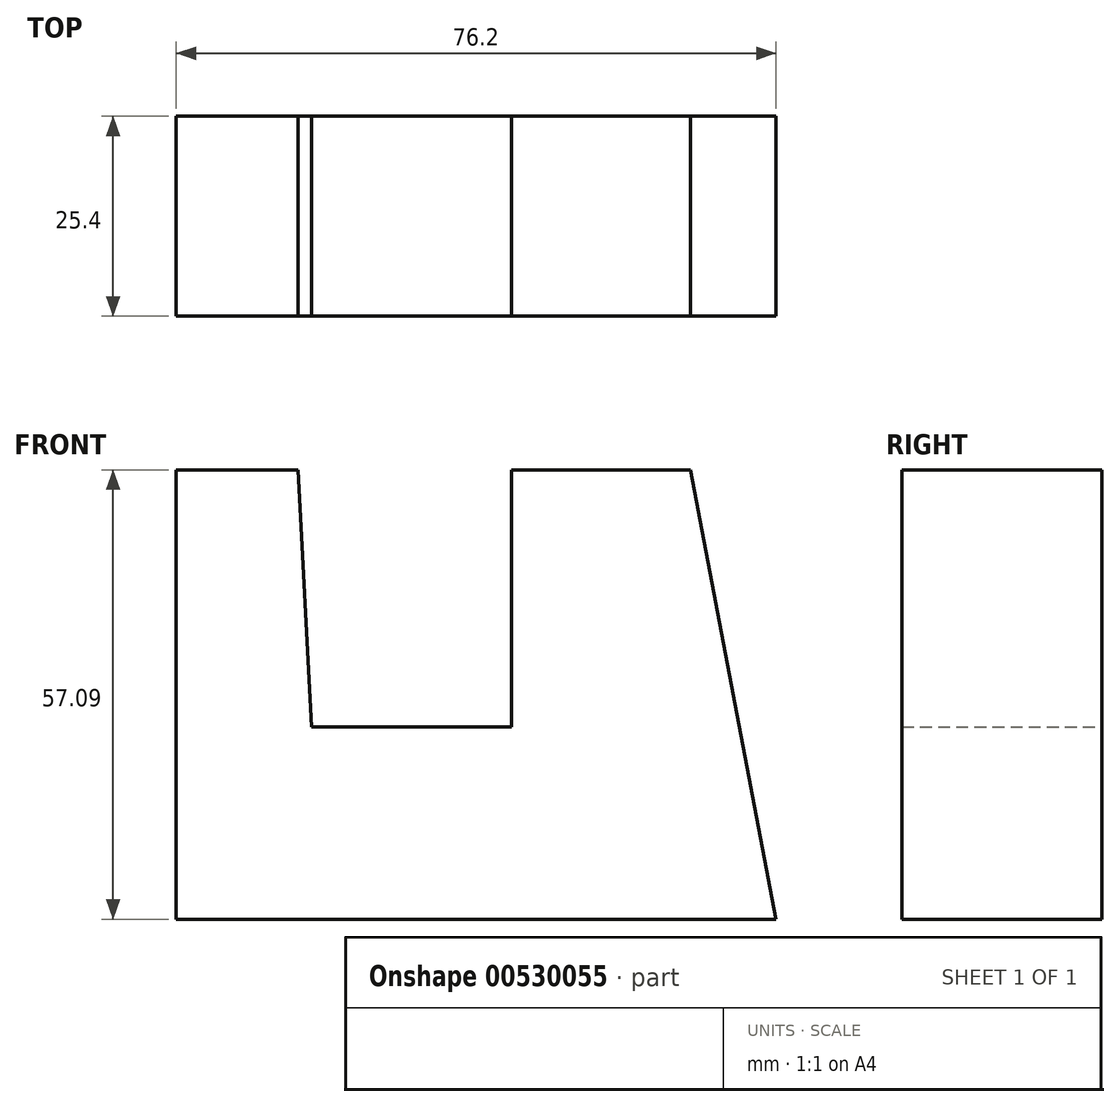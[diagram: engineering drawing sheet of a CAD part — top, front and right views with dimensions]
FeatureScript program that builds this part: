
annotation { "Feature Type Name" : "Feature", "Feature Type Description" : "" }
export const myFeature = defineFeature(function(context is Context, id is Id, definition is map)
    precondition{}
    {
        {
            var Q0;
            Q0=qCreatedBy(makeId("Front.planeOp"),FACE);
            var sketch = newSketch(context, id + "F0", { "sketchPlane" : qUnion([Q0])});
            skLineSegment(sketch, "E0", {"start": v(0, 0) * mm, "end": v(-76.2, 0) * mm});
            skLineSegment(sketch, "E1", {"start": v(-76.2, 0) * mm, "end": v(-76.2, 57.09) * mm});
            skLineSegment(sketch, "E2", {"start": v(-76.2, 57.09) * mm, "end": v(-60.72, 57.09) * mm});
            skLineSegment(sketch, "E3", {"start": v(-60.72, 57.09) * mm, "end": v(-59.02, 24.43) * mm});
            skLineSegment(sketch, "E4", {"start": v(-59.02, 24.43) * mm, "end": v(-33.62, 24.43) * mm});
            skLineSegment(sketch, "E5", {"start": v(-33.62, 24.43) * mm, "end": v(-33.62, 57.09) * mm});
            skLineSegment(sketch, "E6", {"start": v(-33.62, 57.09) * mm, "end": v(-10.89, 57.09) * mm});
            skLineSegment(sketch, "E7", {"start": v(-10.89, 57.09) * mm, "end": v(0, 0) * mm});
            skSolve(sketch);
        }
        {
            var Q0;
            Q0 = qSketchRegion(id + "F0", true);
            extrude(context, id + "F1", {"entities" : qUnion([Q0]), "depth" : 25.4 * mm, "offsetDistance" : 25.4 * mm});
        }
    });
